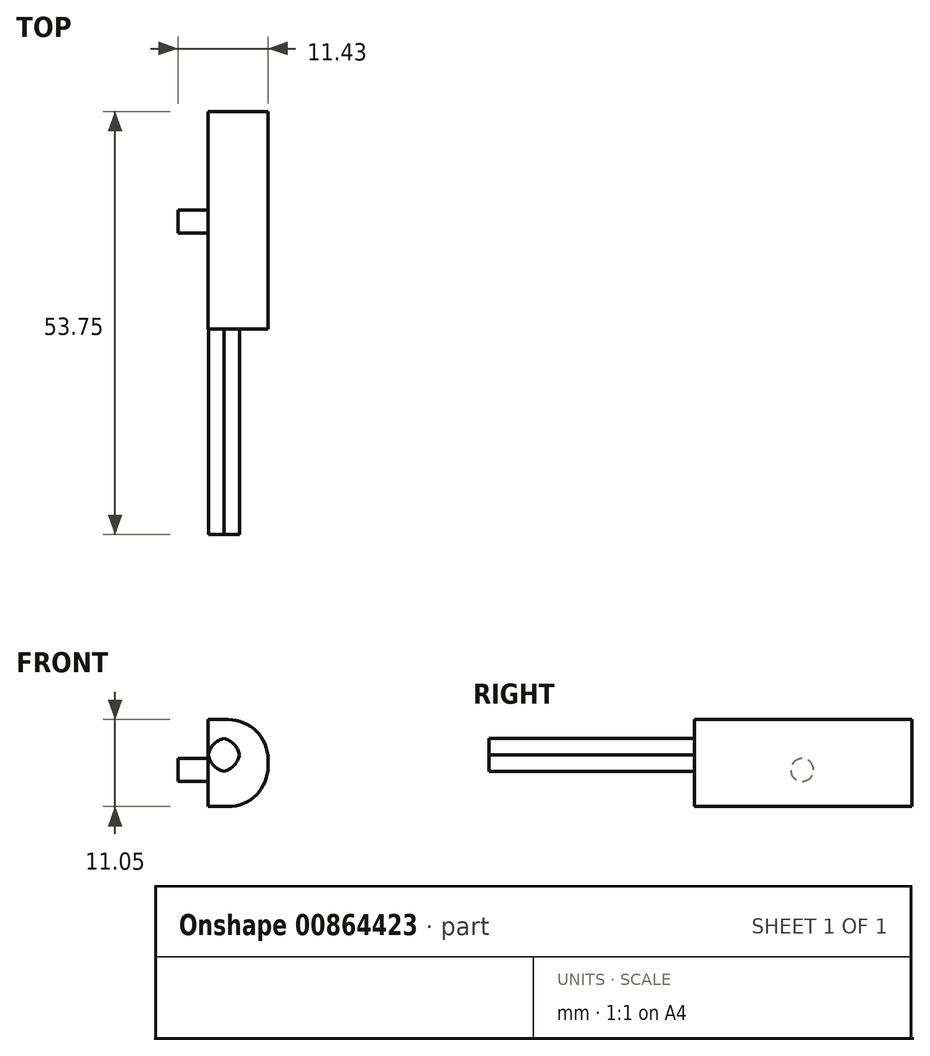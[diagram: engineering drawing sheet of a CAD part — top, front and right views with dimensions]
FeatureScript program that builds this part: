
annotation { "Feature Type Name" : "Feature", "Feature Type Description" : "" }
export const myFeature = defineFeature(function(context is Context, id is Id, definition is map)
    precondition{}
    {
        {
            var Q0;
            Q0=qCreatedBy(makeId("Right.planeOp"),FACE);
            var sketch = newSketch(context, id + "F0", { "sketchPlane" : qUnion([Q0])});
            skLineSegment(sketch, "E0.bottom", {"start": v(0, 26.21) * mm, "end": v(-39.78, 26.21) * mm});
            skLineSegment(sketch, "E0.top", {"start": v(0, 21.95) * mm, "end": v(-39.78, 21.95) * mm});
            skLineSegment(sketch, "E0.left", {"start": v(0, 26.21) * mm, "end": v(0, 21.95) * mm});
            skLineSegment(sketch, "E0.right", {"start": v(-39.78, 26.21) * mm, "end": v(-39.78, 21.95) * mm});
            skSolve(sketch);
        }
        {
            var Q0;
            Q0=makeQuery(id+"F0.imprint","IMPRINT",FACE,{"disambiguationData":[TD([[makeQuery(id+"F0.imprint","IMPRINT",EDGE,{"derivedFrom":sQuery(id+"F0.wireOp",EDGE,"E0.bottom")}),1.0]])]});
            extrude(context, id + "F1", {"entities" : qUnion([Q0]), "depth" : 4 * mm, "offsetDistance" : 25.4 * mm});
        }
        {
            var Q0;
            Q0=makeQuery(id+"F1.opExtrude","CAP_EDGE",EDGE,{"disambiguationData":[OSD([sQuery(id+"F0.wireOp",EDGE,"E0.bottom")])],"isStart":false});
            var Q1;
            Q1=makeQuery(id+"F1.opExtrude","CAP_EDGE",EDGE,{"disambiguationData":[OSD([sQuery(id+"F0.wireOp",EDGE,"E0.bottom")])],"isStart":true});
            var Q2;
            Q2=makeQuery(id+"F1.opExtrude","CAP_EDGE",EDGE,{"disambiguationData":[OSD([sQuery(id+"F0.wireOp",EDGE,"E0.top")])],"isStart":false});
            var Q3;
            Q3=makeQuery(id+"F1.opExtrude","CAP_EDGE",EDGE,{"disambiguationData":[OSD([sQuery(id+"F0.wireOp",EDGE,"E0.top")])],"isStart":true});
            fillet(context, id + "F2", {"entities" : qUnion([Q0, Q1, Q2, Q3]), "radius" : 2.54 * mm, "tangentPropagation" : true, "allowEdgeOverflow" : false});
        }
        {
            var Q0;
            Q0=qCreatedBy(makeId("Right.planeOp"),FACE);
            var sketch = newSketch(context, id + "F3", { "sketchPlane" : qUnion([Q0])});
            skLineSegment(sketch, "E1.bottom", {"start": v(-13.66, 28.57) * mm, "end": v(13.97, 28.57) * mm});
            skLineSegment(sketch, "E1.top", {"start": v(-13.66, 17.52) * mm, "end": v(13.97, 17.52) * mm});
            skLineSegment(sketch, "E1.left", {"start": v(-13.66, 28.57) * mm, "end": v(-13.66, 17.52) * mm});
            skLineSegment(sketch, "E1.right", {"start": v(13.97, 28.57) * mm, "end": v(13.97, 17.52) * mm});
            skSolve(sketch);
        }
        {
            var Q0;
            Q0=makeQuery(id+"F3.imprint","IMPRINT",FACE,{"disambiguationData":[TD([[makeQuery(id+"F3.imprint","IMPRINT",EDGE,{"derivedFrom":sQuery(id+"F3.wireOp",EDGE,"E1.bottom")}),-1.0]])]});
            extrude(context, id + "F4", {"entities" : qUnion([Q0]), "operationType" : NewBodyOperationType.ADD, "depth" : 7.62 * mm, "offsetDistance" : 25.4 * mm});
        }
        {
            var Q0;
            Q0=makeQuery(id+"F4.opExtrude","CAP_EDGE",EDGE,{"disambiguationData":[OSD([sQuery(id+"F3.wireOp",EDGE,"E1.bottom")])],"isStart":false});
            var Q1;
            Q1=makeQuery(id+"F4.opExtrude","CAP_EDGE",EDGE,{"disambiguationData":[OSD([sQuery(id+"F3.wireOp",EDGE,"E1.top")])],"isStart":false});
            fillet(context, id + "F5", {"entities" : qUnion([Q0, Q1]), "radius" : 5.08 * mm, "tangentPropagation" : true, "allowEdgeOverflow" : false});
        }
        {
            var Q0;
            Q0=makeQuery(id+"F4.opExtrude","CAP_FACE",FACE,{"disambiguationData":[OSD([sQuery(id+"F3.wireOp",EDGE,"E1.bottom"),sQuery(id+"F3.wireOp",EDGE,"E1.top"),sQuery(id+"F3.wireOp",EDGE,"E1.left"),sQuery(id+"F3.wireOp",EDGE,"E1.right")])],"isStart":true});
            var sketch = newSketch(context, id + "F6", { "sketchPlane" : qUnion([Q0])});
            skCircle(sketch, "E2", {"center": v(0, 22.16) * mm, "radius": 1.45 * mm});
            skSolve(sketch);
        }
        {
            var Q0;
            Q0=makeQuery(id+"F6.imprint","IMPRINT",FACE,{"disambiguationData":[TD([[makeQuery(id+"F6.imprint","IMPRINT",EDGE,{"derivedFrom":sQuery(id+"F6.wireOp",EDGE,"E2")}),1.0]])]});
            extrude(context, id + "F7", {"entities" : qUnion([Q0]), "operationType" : NewBodyOperationType.ADD, "depth" : 3.8 * mm, "offsetDistance" : 25.4 * mm});
        }
    });
